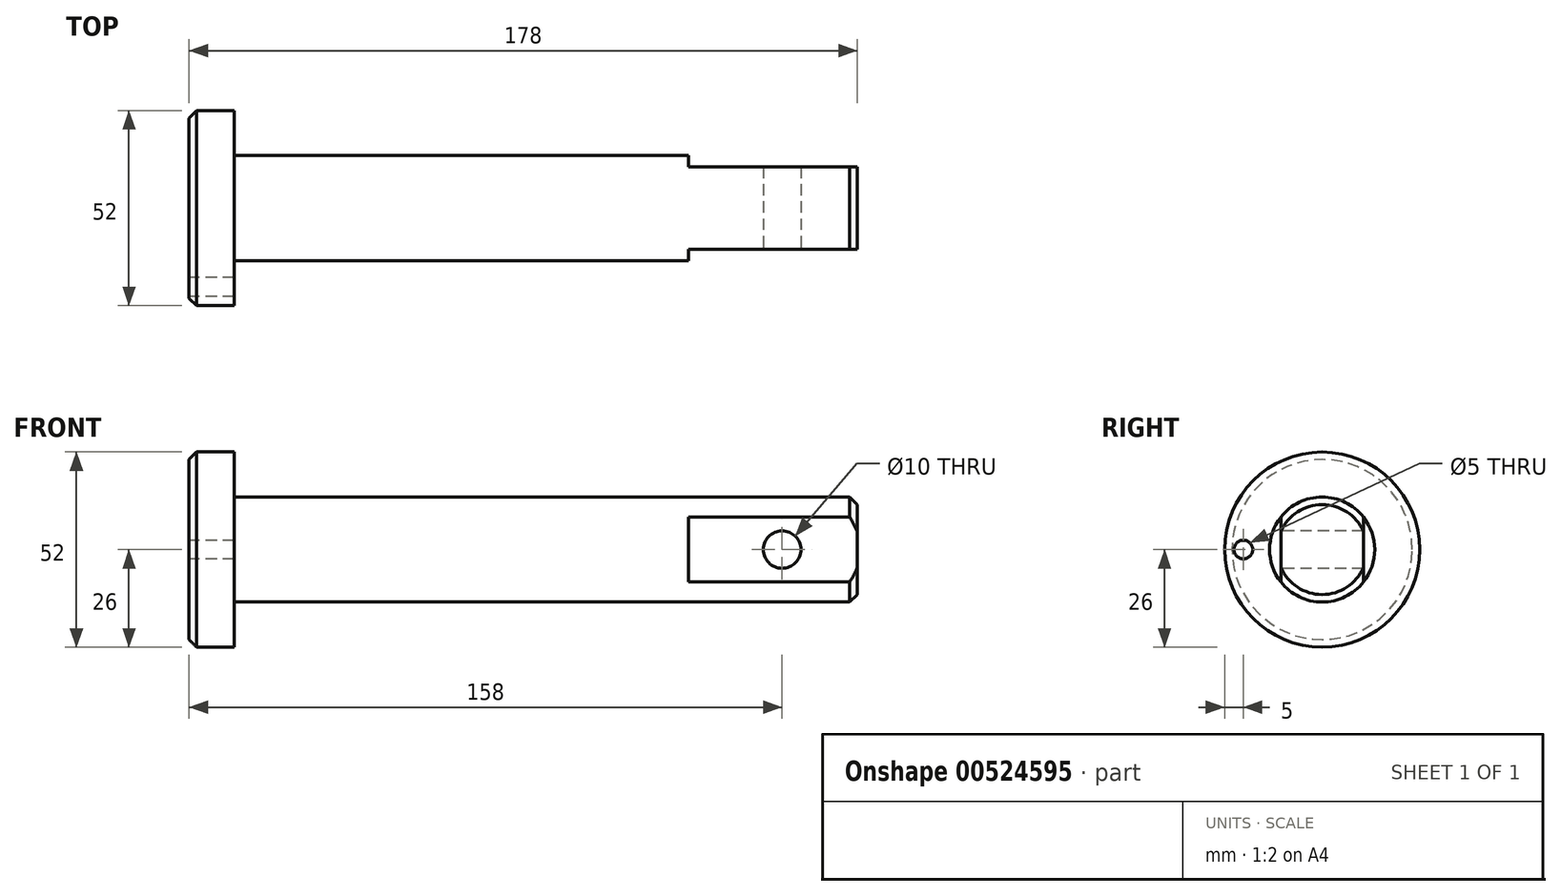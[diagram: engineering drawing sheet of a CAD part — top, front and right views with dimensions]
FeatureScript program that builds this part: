
annotation { "Feature Type Name" : "Feature", "Feature Type Description" : "" }
export const myFeature = defineFeature(function(context is Context, id is Id, definition is map)
    precondition{}
    {
        {
            var Q0;
            Q0=qCreatedBy(makeId("Right.planeOp"),FACE);
            var sketch = newSketch(context, id + "F0", { "sketchPlane" : qUnion([Q0])});
            skCircle(sketch, "E0", {"center": v(0, 0) * mm, "radius": 26 * mm});
            skCircle(sketch, "E1", {"center": v(0, 0) * mm, "radius": 14 * mm});
            skSolve(sketch);
        }
        {
            var Q0;
            Q0 = qSketchRegion(id + "F0", true);
            var Q1;
            Q1=makeQuery(id+"F0.imprint","IMPRINT",FACE,{"disambiguationData":[TD([[makeQuery(id+"F0.imprint","IMPRINT",EDGE,{"derivedFrom":sQuery(id+"F0.wireOp",EDGE,"E1")}),1.0]])]});
            extrude(context, id + "F1", {"entities" : qUnion([Q0, Q1]), "depth" : 12 * mm, "offsetDistance" : 25 * mm});
        }
        {
            var Q0;
            Q0=makeQuery(id+"F0.imprint","IMPRINT",FACE,{"disambiguationData":[TD([[makeQuery(id+"F0.imprint","IMPRINT",EDGE,{"derivedFrom":sQuery(id+"F0.wireOp",EDGE,"E1")}),1.0]])]});
            extrude(context, id + "F2", {"entities" : qUnion([Q0]), "operationType" : NewBodyOperationType.ADD, "depth" : (166 + 12) * mm, "offsetDistance" : 25 * mm});
        }
        {
            var Q0;
            Q0=makeQuery(id+"F1.opExtrude","CAP_EDGE",EDGE,{"disambiguationData":[OSD([sQuery(id+"F0.wireOp",EDGE,"E0")])],"isStart":true});
            var Q1;
            Q1=makeQuery(id+"F2.opExtrude","CAP_EDGE",EDGE,{"disambiguationData":[OSD([sQuery(id+"F0.wireOp",EDGE,"E1")])],"isStart":false});
            chamfer(context, id + "F3", {"entities" : qUnion([Q0, Q1]), "width" : 2 * mm, "tangentPropagation" : true});
        }
        {
            var Q0;
            Q0=makeQuery(id+"F1.opExtrude","CAP_FACE",FACE,{"disambiguationData":[OSD([sQuery(id+"F0.wireOp",EDGE,"E0")])],"isStart":true});
            var sketch = newSketch(context, id + "F4", { "sketchPlane" : qUnion([Q0])});
            skCircle(sketch, "E2", {"center": v(21, 0) * mm, "radius": 2.5 * mm});
            skSolve(sketch);
        }
        {
            var Q0;
            Q0 = qSketchRegion(id + "F4", true);
            extrude(context, id + "F5", {"entities" : qUnion([Q0]), "operationType" : NewBodyOperationType.REMOVE, "endBound" : BoundingType.UP_TO_NEXT, "oppositeDirection" : true, "depth" : 25 * mm, "offsetDistance" : 10 * mm});
        }
        {
            var Q0;
            Q0=makeQuery(id+"F2.opExtrude","CAP_FACE",FACE,{"disambiguationData":[OSD([sQuery(id+"F0.wireOp",EDGE,"E1")])],"isStart":false});
            var sketch = newSketch(context, id + "F6", { "sketchPlane" : qUnion([Q0])});
            skCircle(sketch, "E3.0", {"center": v(0, 0) * mm, "radius": 14 * mm});
            skLineSegment(sketch, "E4", {"start": v(0, 0) * mm, "end": v(0, -7.07) * mm, "construction": true});
            skLineSegment(sketch, "E5", {"start": v(11, 8.66) * mm, "end": v(11, -8.66) * mm});
            skLineSegment(sketch, "E6.MirrorCS", {"start": v(-11, 8.66) * mm, "end": v(-11, -8.66) * mm});
            skSolve(sketch);
        }
        {
            var Q0;
            {var subQ0=sQuery(id+"F6.wireOp",EDGE,"E6.MirrorCS");var subQ1=sQuery(id+"F6.wireOp",EDGE,"E3.0");var subQ2=makeQuery(id+"F6.imprint","INTERSECT",VERTEX,{"disambiguationData":[OD(0.0)],"derivedFrom":[subQ1,subQ0]});Q0=makeQuery(id+"F6.imprint","IMPRINT",FACE,{"disambiguationData":[TD([[makeQuery(id+"F6.imprint","IMPRINT",EDGE,{"disambiguationData":[TD([[subQ2,-1.0]])],"derivedFrom":subQ1}),1.0]])]});}
            var Q1;
            {var subQ0=sQuery(id+"F6.wireOp",EDGE,"E6.MirrorCS");var subQ1=sQuery(id+"F0.wireOp",EDGE,"E1");var subQ2=makeQuery(id+"F3.opChamfer","BLEND_EDGE",EDGE,{"blendedFrom":[makeQuery(id+"F2.opExtrude","CAP_EDGE",EDGE,{"disambiguationData":[OSD([subQ1])],"isStart":false}),makeQuery(id+"F2.opExtrude","CAP_FACE",FACE,{"disambiguationData":[OSD([subQ1])],"isStart":false})],"blendedInto":[makeQuery(id+"F2.opExtrude","CAP_FACE",FACE,{"disambiguationData":[OSD([subQ1])],"isStart":false})]});var subQ3=makeQuery(id+"F6.imprint","INTERSECT",VERTEX,{"disambiguationData":[OD(0.0)],"derivedFrom":[subQ2,subQ0]});Q1=makeQuery(id+"F6.imprint","IMPRINT",FACE,{"disambiguationData":[TD([[makeQuery(id+"F6.imprint","IMPRINT",EDGE,{"disambiguationData":[TD([[subQ3,-1.0]])],"derivedFrom":subQ0}),-1.0]])]});}
            var Q2;
            {var subQ0=sQuery(id+"F6.wireOp",EDGE,"E5");var subQ1=sQuery(id+"F0.wireOp",EDGE,"E1");var subQ2=makeQuery(id+"F3.opChamfer","BLEND_EDGE",EDGE,{"blendedFrom":[makeQuery(id+"F2.opExtrude","CAP_EDGE",EDGE,{"disambiguationData":[OSD([subQ1])],"isStart":false}),makeQuery(id+"F2.opExtrude","CAP_FACE",FACE,{"disambiguationData":[OSD([subQ1])],"isStart":false})],"blendedInto":[makeQuery(id+"F2.opExtrude","CAP_FACE",FACE,{"disambiguationData":[OSD([subQ1])],"isStart":false})]});var subQ3=makeQuery(id+"F6.imprint","INTERSECT",VERTEX,{"disambiguationData":[OD(0.0)],"derivedFrom":[subQ2,subQ0]});Q2=makeQuery(id+"F6.imprint","IMPRINT",FACE,{"disambiguationData":[TD([[makeQuery(id+"F6.imprint","IMPRINT",EDGE,{"disambiguationData":[TD([[subQ3,-1.0]])],"derivedFrom":subQ0}),1.0]])]});}
            var Q3;
            {var subQ0=sQuery(id+"F6.wireOp",EDGE,"E5");var subQ1=sQuery(id+"F6.wireOp",EDGE,"E3.0");var subQ2=makeQuery(id+"F6.imprint","INTERSECT",VERTEX,{"disambiguationData":[OD(0.0)],"derivedFrom":[subQ1,subQ0]});Q3=makeQuery(id+"F6.imprint","IMPRINT",FACE,{"disambiguationData":[TD([[makeQuery(id+"F6.imprint","IMPRINT",EDGE,{"disambiguationData":[TD([[subQ2,1.0]])],"derivedFrom":subQ1}),1.0]])]});}
            extrude(context, id + "F7", {"entities" : qUnion([Q0, Q1, Q2, Q3]), "operationType" : NewBodyOperationType.REMOVE, "oppositeDirection" : true, "depth" : 45 * mm, "offsetDistance" : 25 * mm});
        }
        {
            var Q0;
            Q0=makeQuery(id+"F7.boolean.opBoolean","COPY",FACE,{"derivedFrom":makeQuery(id+"F7.opExtrude","SWEPT_FACE",FACE,{"disambiguationData":[OSD([sQuery(id+"F6.wireOp",EDGE,"E6.MirrorCS")])]})});
            var sketch = newSketch(context, id + "F8", { "sketchPlane" : qUnion([Q0])});
            skCircle(sketch, "E7", {"center": v(158, 0) * mm, "radius": 5 * mm});
            skPoint(sketch, "E7.centerSnap0", {"position": v(178, 0) * mm});
            skSolve(sketch);
        }
        {
            var Q0;
            Q0 = qSketchRegion(id + "F8", true);
            extrude(context, id + "F9", {"entities" : qUnion([Q0]), "operationType" : NewBodyOperationType.REMOVE, "endBound" : BoundingType.UP_TO_NEXT, "oppositeDirection" : true, "depth" : 25 * mm, "offsetDistance" : 25 * mm});
        }
    });
